# Revit family: VV5005551_Grifería para Lavaplatos Vaal 8 Pulgadas
name_source: partatom
category: Plumbing Fixtures
units: mm (PartAtom-declared; Revit-internal decimal feet)

## family parameters
Always vertical = Yes
Cut with Voids When Loaded = No
OmniClass Number = 23.21.21.19
OmniClass Title = Commercial Dishwasher Equipment
Part Type = Normal
Room Calculation Point = No
Round Connector Dimension = Use Diameter
Shared = No
Work Plane-Based = No

## types (1)
- VV5005551_Grifería para Lavaplatos Vaal 8 Pulgadas
    Acabado = Cromado
    Alto = 40.13 cm
    Ancho = 4.41 cm
    Capacidad de flujo = 6.96 l/m máximo a 60 psi
    Colección = Vida 2014
    Consumo de agua = 6.96 lt
    Creado por = IDD
    Description = Este producto ha sido diseñado para trabajar en perfecta armonía con el espacio, ofreciendo un producto robusto y funcional. Con pico giratorio que le permite al usuario tomar ventaja del área del lavaplatos.
    Fecha de creación = 22/07/2020
    Incluye = Cuerpo, pico, manijas
    Largo = 21.9 cm
    Línea = Vaal
    Material = Corona_Cromado
    Materiales = Metal
    Productos compatibles = Lavaplatos
    Rango de presión de agua = Entre 20 y 125 psi
    Resistencia = Resistente a la corrosión pelado y decoloración por agua
    Sistema de accionamiento = Palanca
    Temperatura de uso = Entre 4˚C y 66˚C
    Tipo de chorro = Espumoso
    Tipo de grifería = 8 pulgadas
    Tipo de manija/accionamiento = Palanca
    URL = https://corona.co
    Uso = Residencial

## geometry (parser evidence)
native form markers: Sweep x5
no freeform markers — native parametric forms only
